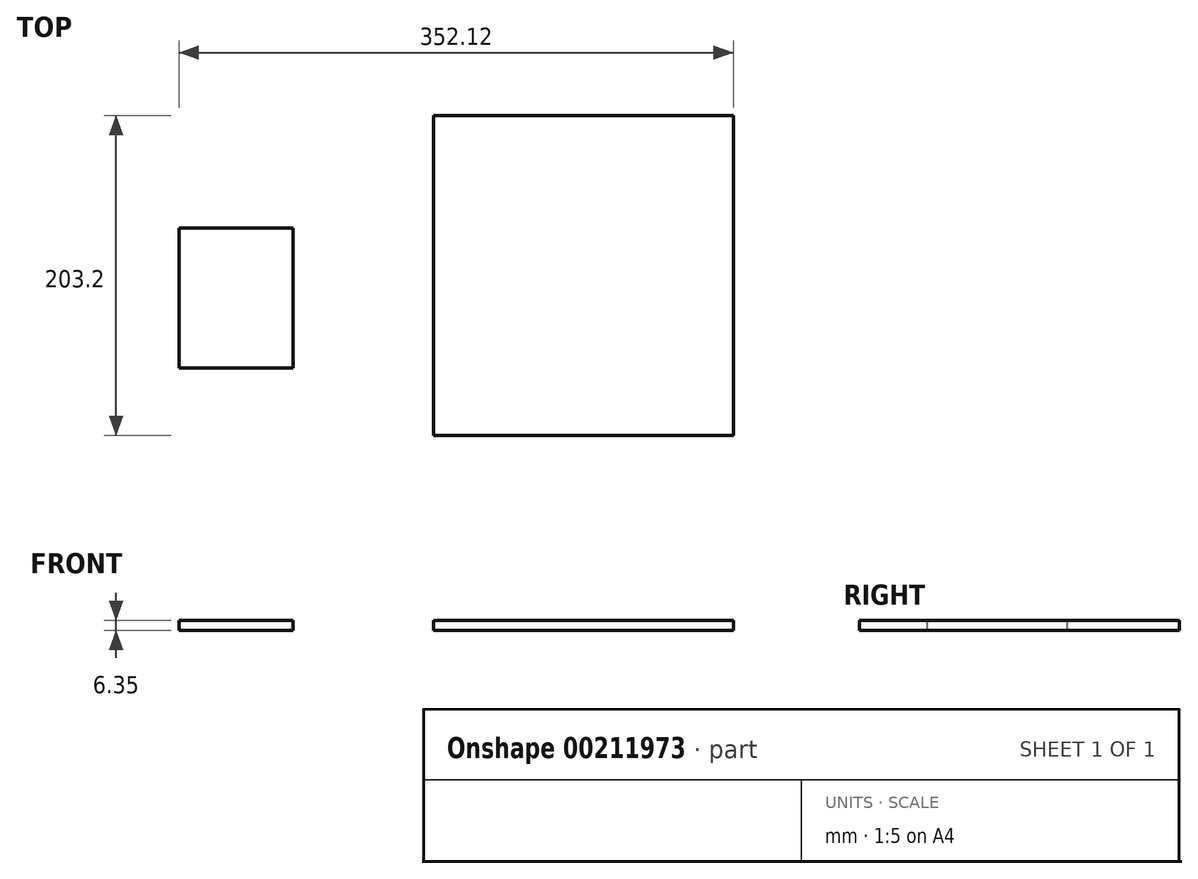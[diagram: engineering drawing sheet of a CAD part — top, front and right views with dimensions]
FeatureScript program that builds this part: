
annotation { "Feature Type Name" : "Feature", "Feature Type Description" : "" }
export const myFeature = defineFeature(function(context is Context, id is Id, definition is map)
    precondition{}
    {
        {
            var Q0;
            Q0=qCreatedBy(makeId("Top.planeOp"),FACE);
            var sketch = newSketch(context, id + "F0", { "sketchPlane" : qUnion([Q0])});
            skLineSegment(sketch, "E0.bottom", {"start": v(95.25, -101.6) * mm, "end": v(-95.25, -101.6) * mm});
            skLineSegment(sketch, "E0.top", {"start": v(95.25, 101.6) * mm, "end": v(-95.25, 101.6) * mm});
            skLineSegment(sketch, "E0.left", {"start": v(95.25, -101.6) * mm, "end": v(95.25, 101.6) * mm});
            skLineSegment(sketch, "E0.right", {"start": v(-95.25, -101.6) * mm, "end": v(-95.25, 101.6) * mm});
            skPoint(sketch, "E0.middle", {"position": v(0, 0) * mm});
            skLineSegment(sketch, "E1.bottom", {"start": v(-184.33, 30.17) * mm, "end": v(-256.87, 30.17) * mm});
            skLineSegment(sketch, "E1.top", {"start": v(-184.33, -58.73) * mm, "end": v(-256.87, -58.73) * mm});
            skLineSegment(sketch, "E1.left", {"start": v(-184.33, 30.17) * mm, "end": v(-184.33, -58.73) * mm});
            skLineSegment(sketch, "E1.right", {"start": v(-256.87, 30.17) * mm, "end": v(-256.87, -58.73) * mm});
            skSolve(sketch);
        }
        {
            var Q0;
            Q0=makeQuery(id+"F0.imprint","IMPRINT",FACE,{"disambiguationData":[TD([[makeQuery(id+"F0.imprint","IMPRINT",EDGE,{"derivedFrom":sQuery(id+"F0.wireOp",EDGE,"E0.bottom")}),-1.0]])]});
            var Q1;
            Q1=makeQuery(id+"F0.imprint","IMPRINT",FACE,{"disambiguationData":[TD([[makeQuery(id+"F0.imprint","IMPRINT",EDGE,{"derivedFrom":sQuery(id+"F0.wireOp",EDGE,"E1.bottom")}),1.0]])]});
            extrude(context, id + "F1", {"entities" : qUnion([Q0, Q1]), "depth" : 6.35 * mm});
        }
    });
